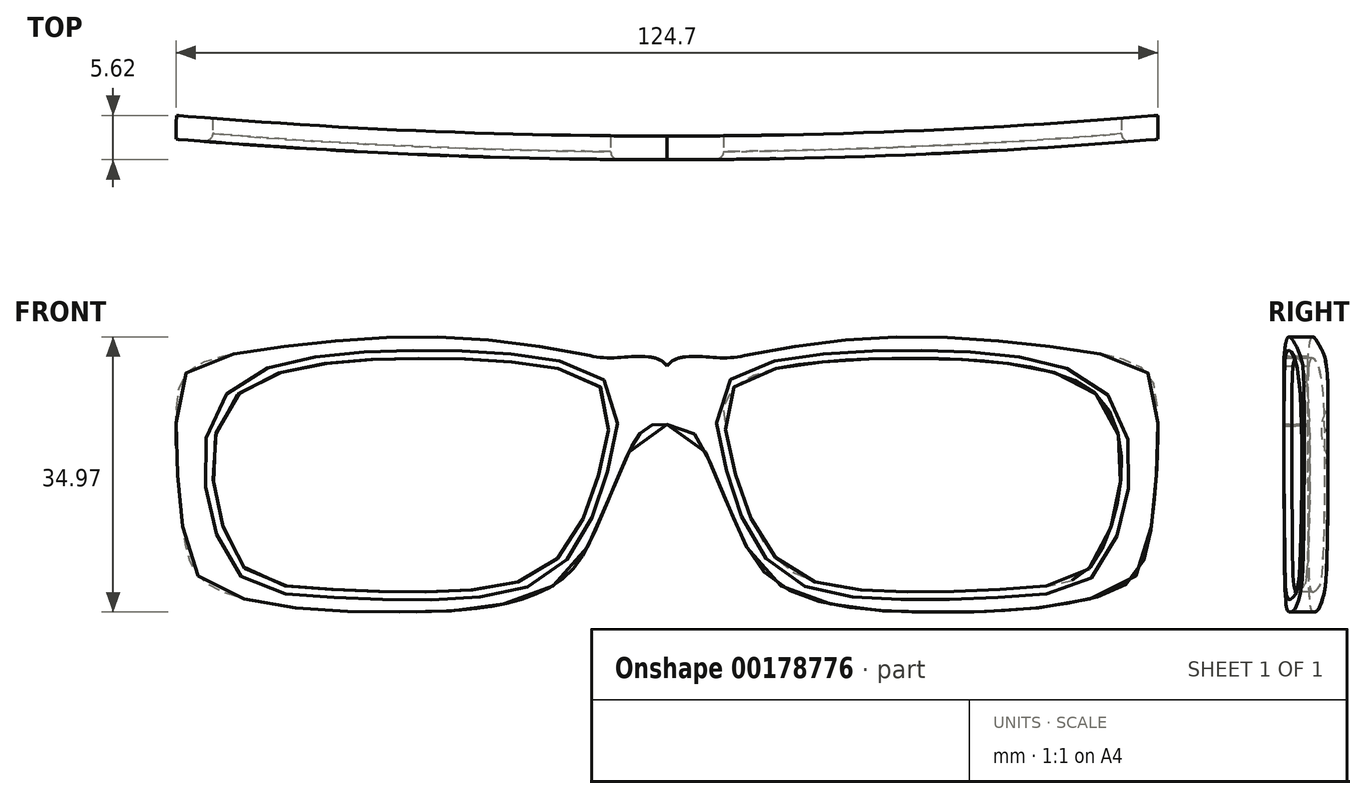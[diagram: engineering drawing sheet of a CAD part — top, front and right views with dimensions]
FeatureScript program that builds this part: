
annotation { "Feature Type Name" : "Feature", "Feature Type Description" : "" }
export const myFeature = defineFeature(function(context is Context, id is Id, definition is map)
    precondition{}
    {
        {
            var Q0;
            Q0=qCreatedBy(makeId("Front.planeOp"),FACE);
            var sketch = newSketch(context, id + "F0", { "sketchPlane" : qUnion([Q0])});
            skFitSpline(sketch, "E0", {"points": [v(13.87, 13.45) * mm, v(37.18, 14.63) * mm, v(53.97, 10.65) * mm, v(57.6, 3.46) * mm, v(56.6, -5.94) * mm, v(52.68, -12.77) * mm, v(46.86, -14.27) * mm, v(37.68, -14.8) * mm, v(19.2, -13.74) * mm, v(12.96, -9.54) * mm, v(9.6, -2.92) * mm, v(7.57, 5.03) * mm, v(7.38, 9.84) * mm, v(9.11, 11.54) * mm, v(13.87, 13.45) * mm]});
            skFitSpline(sketch, "E1", {"points": [v(0, 13.79) * mm, v(6.56, 14.83) * mm, v(12.38, 15.62) * mm, v(28.88, 17.46) * mm, v(48.77, 16.26) * mm, v(60.32, 13.56) * mm, v(62.27, 8.73) * mm, v(61.03, -9.32) * mm, v(57.84, -14.26) * mm, v(46.91, -16.95) * mm, v(35.16, -17.46) * mm, v(21.65, -16.64) * mm, v(13.1, -13.13) * mm, v(9.28, -7.46) * mm, v(5.56, 1.3) * mm, v(4.01, 4.4) * mm, v(1.85, 6.34) * mm, v(0, 6.37) * mm, v(0, 13.79) * mm]});
            skFitSpline(sketch, "E2", {"points": [v(0, 13.79) * mm, v(3.17, 13.79) * mm, v(7, 14.45) * mm, v(9.81, 15.1) * mm], "startDerivative": vector(9.38, -0.45) * mm, "endDerivative": vector(8.6, 2.02) * mm});
            skFitSpline(sketch, "E3.MirrorCS", {"points": [v(0, 13.79) * mm, v(-3.17, 13.79) * mm, v(-7, 14.45) * mm, v(-9.81, 15.1) * mm], "startDerivative": vector(-9.38, -0.45) * mm, "endDerivative": vector(-8.6, 2.02) * mm});
            skFitSpline(sketch, "E4.MirrorCS", {"points": [v(0, 13.79) * mm, v(-6.56, 14.83) * mm, v(-12.38, 15.62) * mm, v(-28.88, 17.46) * mm, v(-48.77, 16.26) * mm, v(-60.32, 13.56) * mm, v(-62.27, 8.73) * mm, v(-61.03, -9.32) * mm, v(-57.84, -14.26) * mm, v(-46.91, -16.95) * mm, v(-35.16, -17.46) * mm, v(-21.65, -16.64) * mm, v(-13.1, -13.13) * mm, v(-9.28, -7.46) * mm, v(-5.56, 1.3) * mm, v(-4.01, 4.4) * mm, v(-1.85, 6.34) * mm, v(0, 6.37) * mm, v(0, 13.79) * mm]});
            skFitSpline(sketch, "E5.MirrorC", {"points": [v(-13.87, 13.45) * mm, v(-37.18, 14.63) * mm, v(-53.97, 10.65) * mm, v(-57.6, 3.46) * mm, v(-56.6, -5.94) * mm, v(-52.68, -12.77) * mm, v(-46.86, -14.27) * mm, v(-37.68, -14.8) * mm, v(-19.2, -13.74) * mm, v(-12.96, -9.54) * mm, v(-9.6, -2.92) * mm, v(-7.57, 5.03) * mm, v(-7.38, 9.84) * mm, v(-9.11, 11.54) * mm, v(-13.87, 13.45) * mm]});
            skSolve(sketch);
        }
        {
            var Q0;
            Q0 = qSketchRegion(id + "F0", true);
            extrude(context, id + "F1", {"entities" : qUnion([Q0]), "endBound" : BoundingType.SYMMETRIC, "depth" : 15 * mm});
        }
        {
            var Q0;
            Q0=qCreatedBy(makeId("Top.planeOp"),FACE);
            var sketch = newSketch(context, id + "F2", { "sketchPlane" : qUnion([Q0])});
            skArc(sketch, "E6", {"start": v(-62.29, 0) * mm, "mid": v(0.03, -2.62) * mm, "end": v(62.35, 0) * mm});
            skArc(sketch, "E7.0", {"start": v(-62.54, -2.99) * mm, "mid": v(0.03, -5.62) * mm, "end": v(62.6, -2.99) * mm});
            skLineSegment(sketch, "E8", {"start": v(-62.54, -2.99) * mm, "end": v(-62.29, 0) * mm});
            skLineSegment(sketch, "E9", {"start": v(62.6, -2.99) * mm, "end": v(62.35, 0) * mm});
            skArc(sketch, "E10.0", {"start": v(-67.94, -7.54) * mm, "mid": v(0.03, -10.62) * mm, "end": v(68, -7.54) * mm});
            skLineSegment(sketch, "E10.1", {"start": v(-67.94, -7.54) * mm, "end": v(-66.85, 5.42) * mm});
            skLineSegment(sketch, "E10.3", {"start": v(68, -7.54) * mm, "end": v(66.91, 5.42) * mm});
            skLineSegment(sketch, "E11", {"start": v(-66.85, 5.42) * mm, "end": v(-49.76, 19.3) * mm});
            skLineSegment(sketch, "E12", {"start": v(-49.76, 19.3) * mm, "end": v(64.4, 12.11) * mm});
            skLineSegment(sketch, "E13", {"start": v(64.4, 12.11) * mm, "end": v(66.91, 5.42) * mm});
            skSolve(sketch);
        }
        {
            var Q0;
            Q0 = qSketchRegion(id + "F2", true);
            extrude(context, id + "F3", {"entities" : qUnion([Q0]), "operationType" : NewBodyOperationType.REMOVE, "endBound" : BoundingType.SYMMETRIC, "depth" : 50 * mm});
        }
        {
            var Q0;
            Q0=makeQuery(id+"F3.boolean.opBoolean","INTERSECT",EDGE,{"derivedFrom":[makeQuery(id+"F1.opExtrude","SWEPT_FACE",FACE,{"disambiguationData":[OSD([sQuery(id+"F0.wireOp",EDGE,"E5.MirrorC")])]}),makeQuery(id+"F3.opExtrude","SWEPT_FACE",FACE,{"disambiguationData":[OSD([sQuery(id+"F2.wireOp",EDGE,"E7.0")])]})]});
            fillet(context, id + "F4", {"entities" : qUnion([Q0]), "radius" : 1 * mm, "tangentPropagation" : true, "allowEdgeOverflow" : false});
        }
        {
            var Q0;
            Q0=makeQuery(id+"F3.boolean.opBoolean","INTERSECT",EDGE,{"derivedFrom":[makeQuery(id+"F1.opExtrude","SWEPT_FACE",FACE,{"disambiguationData":[OSD([sQuery(id+"F0.wireOp",EDGE,"E0")])]}),makeQuery(id+"F3.opExtrude","SWEPT_FACE",FACE,{"disambiguationData":[OSD([sQuery(id+"F2.wireOp",EDGE,"E7.0")])]})]});
            fillet(context, id + "F5", {"entities" : qUnion([Q0]), "radius" : 1 * mm, "tangentPropagation" : true, "allowEdgeOverflow" : false});
        }
    });
